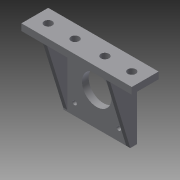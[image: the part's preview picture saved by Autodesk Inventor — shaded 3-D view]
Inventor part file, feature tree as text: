
AUTODESK INVENTOR PART (.ipt)
format: ipt  version: 2014 SP1 (Build 180222100, 222)  size: 159,232 bytes
history: native  units: mm
features: extrude x4, sketch x4
ambient origin geometry x8: Origin, YZ Plane, XZ Plane, XY Plane, X Axis, Y Axis, Z Axis, Center Point
bodies: Solid1 (feature_tree)
feature tree (8):
  extrude  "Extrusion1"  Depth=20.0mm
  extrude  "Extrusion2"  Depth=21.15mm
  extrude  "Extrusion3"  Depth=10.0mm
  extrude  "Extrusion4"  Depth=3.0mm
  sketch  "Sketch1"  dims[d0=82.3mm d1=20.0mm]
  sketch  "Sketch2"  dims[d2=21.15mm d3=21.15mm]
  sketch  "Sketch3"  dims[d4=10.0mm d5=6.0mm]
  sketch  "Sketch4"  dims[d6=10.0mm d7=6.0mm d8=10.0mm d9=10.0mm d10=6.0mm d11=6.0mm d12=5.0mm d13=0.0mm d14=25.0mm d15=50.0mm d16=50.0mm d17=22.0mm d20=16.5mm d22=3.2mm d23=3.2mm d24=3.2mm d25=3.2mm d26=5.0mm d27=0.0mm d28=3.0mm d29=0.0mm d30=3.0mm d31=0.0mm]
